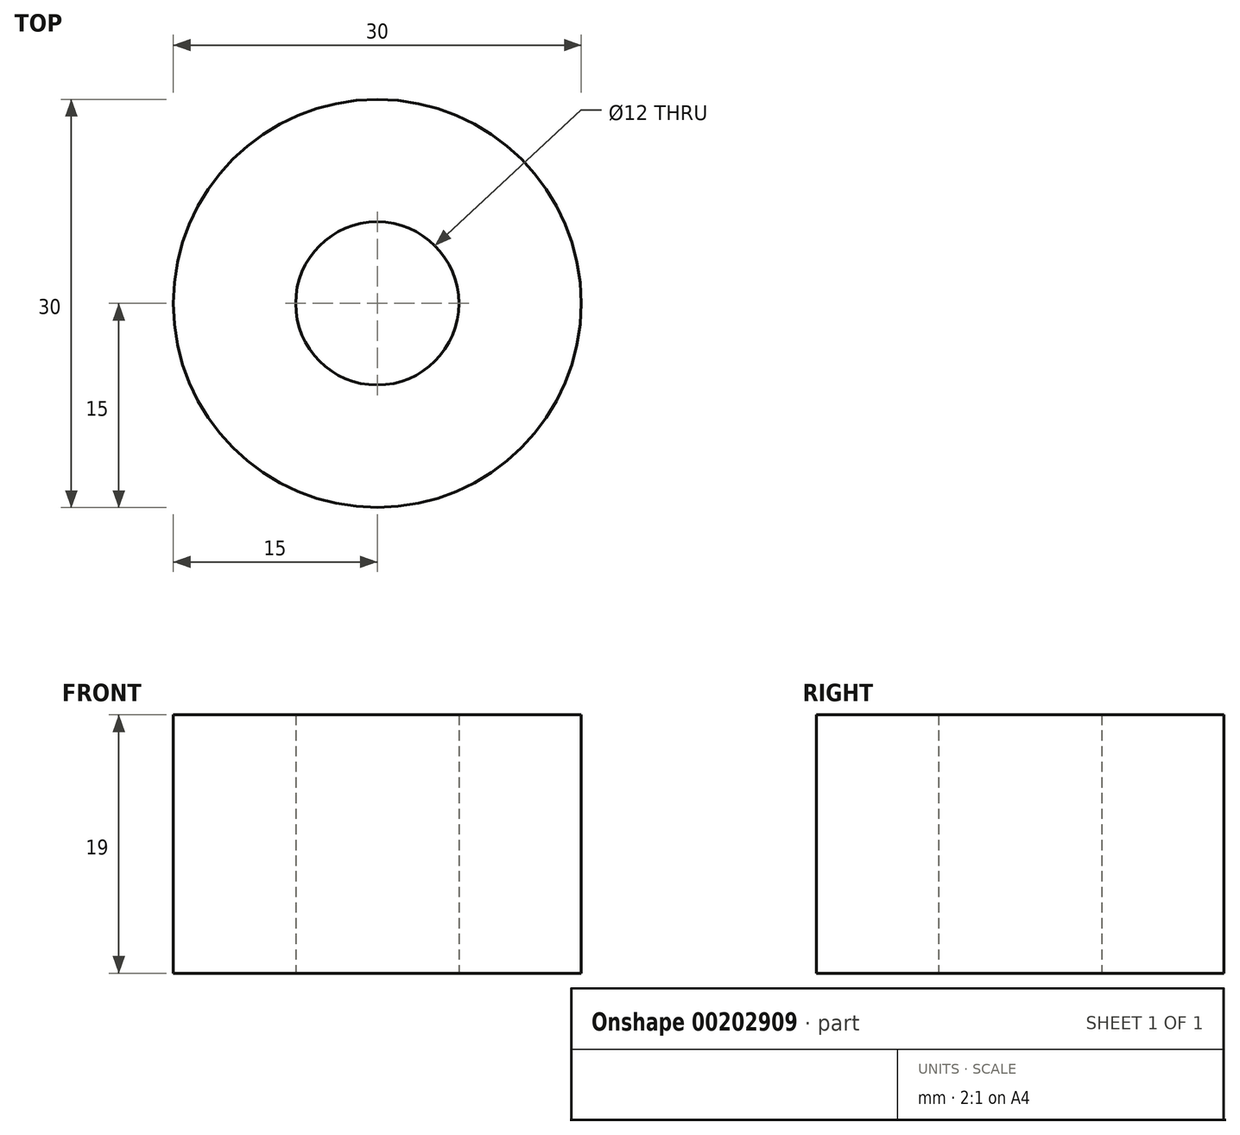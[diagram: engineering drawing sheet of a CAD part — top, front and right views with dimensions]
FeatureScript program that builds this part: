
annotation { "Feature Type Name" : "Feature", "Feature Type Description" : "" }
export const myFeature = defineFeature(function(context is Context, id is Id, definition is map)
    precondition{}
    {
        {
            var Q0;
            Q0=qCreatedBy(makeId("Top.planeOp"),FACE);
            var sketch = newSketch(context, id + "F0", { "sketchPlane" : qUnion([Q0])});
            skCircle(sketch, "E0", {"center": v(0, 0) * mm, "radius": 15 * mm});
            skCircle(sketch, "E1", {"center": v(0, 0) * mm, "radius": 6 * mm});
            skSolve(sketch);
        }
        {
            var Q0;
            Q0=makeQuery(id+"F0.imprint","IMPRINT",FACE,{"disambiguationData":[TD([[makeQuery(id+"F0.imprint","IMPRINT",EDGE,{"derivedFrom":sQuery(id+"F0.wireOp",EDGE,"E0")}),1.0]])]});
            extrude(context, id + "F1", {"entities" : qUnion([Q0]), "depth" : 19 * mm});
        }
    });
